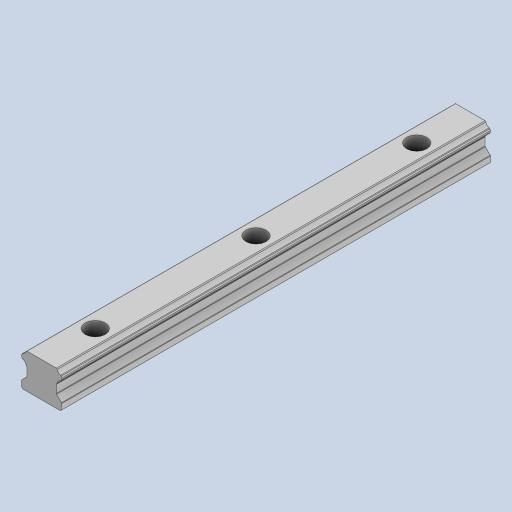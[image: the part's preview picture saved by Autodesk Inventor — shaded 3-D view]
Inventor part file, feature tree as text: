
AUTODESK INVENTOR PART (.ipt)
format: ipt  version: 2023 (Build 270158000, 158)  size: 192,000 bytes
history: native  units: mm
features: other x14, sketch x2, extrude x1, hole x1, pattern_linear x1
ambient origin geometry x8: Origin, YZ Plane, XZ Plane, XY Plane, X Axis, Y Axis, Z Axis, Center Point
bodies: Solid1 (feature_tree)
feature tree (19):
  extrude  "Extrusion1"  Depth=10.0mm TaperAngle=0.0deg
  hole  "Hole1"  [1 undecoded]
  pattern_linear  "Rectangular Pattern1"  [2 undecoded]
  other  "to_block_1_XY"
  other  "to_block_1_YZ"
  other  "to_block_1_ZX"
  other  "to_block_1_X"
  other  "to_block_1_Y"
  other  "to_block_1_Z"
  other  "to_block_1_Center"
  other  "to_block_2_XY"
  other  "to_block_2_YZ"
  other  "to_block_2_ZX"
  other  "to_block_2_X"
  other  "to_block_2_Y"
  other  "to_block_2_Z"
  other  "to_block_2_Center"
  sketch  "Sketch_2"  dims[d0=160.0mm d1=0.0mm]
  sketch  "Sketch2"  dims[d2=4.5mm d3=6.0mm d4=7.5mm d5=6.0mm d6=90.0deg d7=13.0mm d8=0.0mm d9=30.0mm d11=60.0mm d12=10.0mm d14=0.0mm]
note: 3 required parameter values undecoded (feature->parameter linkage not recoverable at this tier; creation-order binding heuristic only, values carry confidence <= 0.55)
